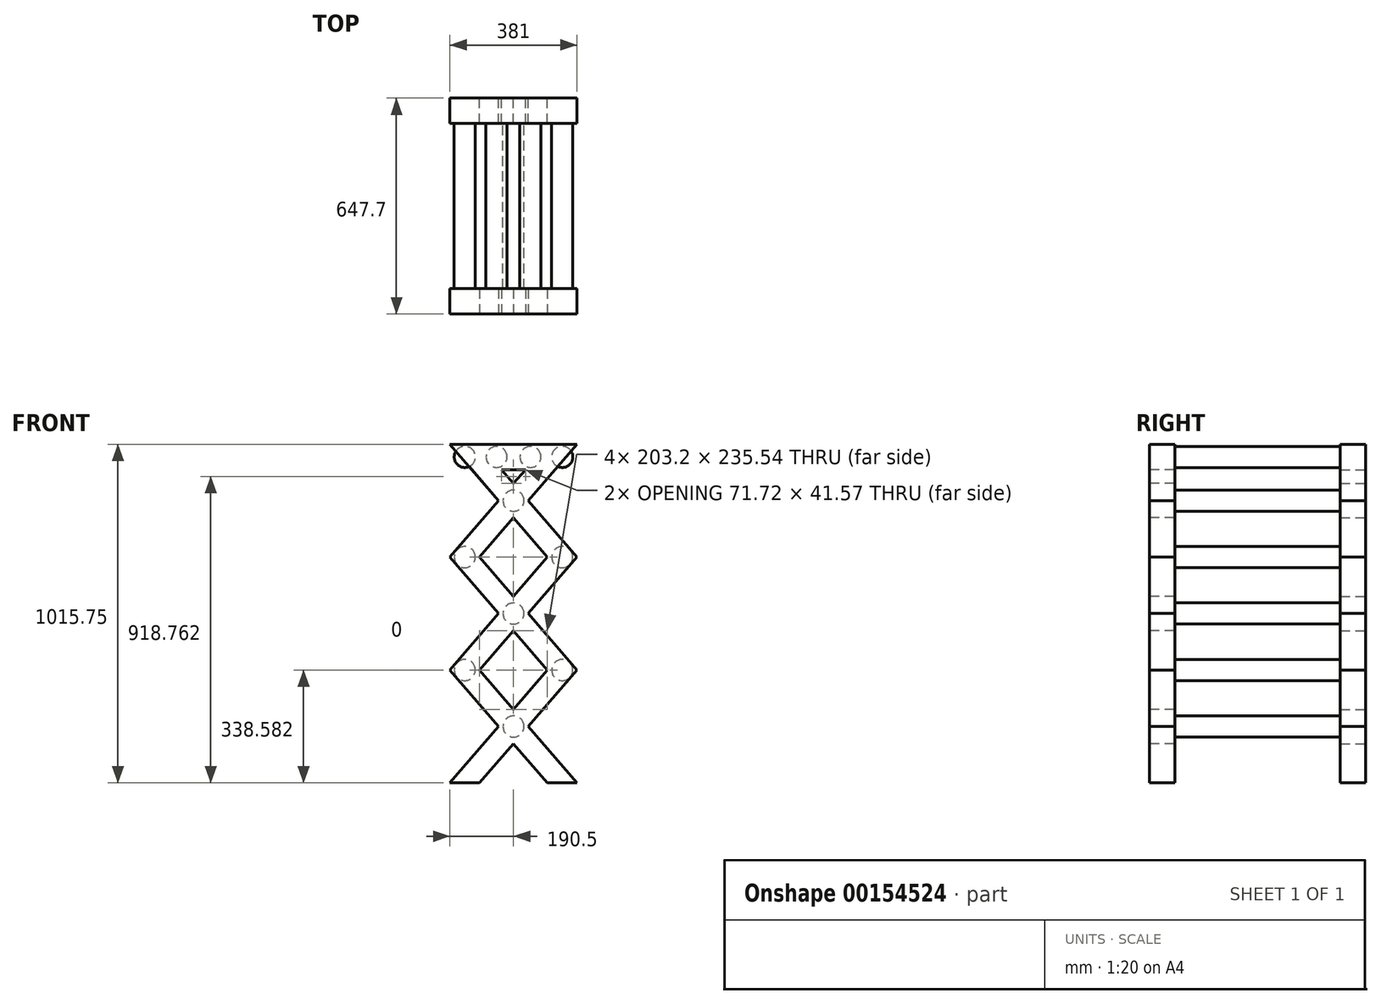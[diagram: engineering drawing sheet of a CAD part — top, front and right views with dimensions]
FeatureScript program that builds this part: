
annotation { "Feature Type Name" : "Feature", "Feature Type Description" : "" }
export const myFeature = defineFeature(function(context is Context, id is Id, definition is map)
    precondition{}
    {
        {
            var Q0;
            Q0=qCreatedBy(makeId("Front.planeOp"),FACE);
            var sketch = newSketch(context, id + "F0", { "sketchPlane" : qUnion([Q0])});
            skLineSegment(sketch, "E0", {"start": v(0, 0) * mm, "end": v(-292.1, 338.58) * mm});
            skLineSegment(sketch, "E1", {"start": v(-292.1, 338.58) * mm, "end": v(-381, 338.58) * mm});
            skLineSegment(sketch, "E2", {"start": v(-381, 338.58) * mm, "end": v(-88.9, 0) * mm});
            skLineSegment(sketch, "E3", {"start": v(-88.9, 0) * mm, "end": v(0, 0) * mm});
            skLineSegment(sketch, "E4", {"start": v(-292.1, 0) * mm, "end": v(0, 338.58) * mm});
            skLineSegment(sketch, "E5", {"start": v(0, 338.58) * mm, "end": v(-88.9, 338.58) * mm});
            skLineSegment(sketch, "E6", {"start": v(-88.9, 338.58) * mm, "end": v(-381, 0) * mm});
            skLineSegment(sketch, "E7", {"start": v(-381, 0) * mm, "end": v(-292.1, 0) * mm});
            skLineSegment(sketch, "E8.MirrorCS", {"start": v(0, 677.16) * mm, "end": v(-292.1, 338.58) * mm});
            skLineSegment(sketch, "E9.MirrorCS", {"start": v(-381, 338.58) * mm, "end": v(-88.9, 677.16) * mm});
            skLineSegment(sketch, "E10.MirrorCS", {"start": v(-88.9, 338.58) * mm, "end": v(-381, 677.16) * mm});
            skLineSegment(sketch, "E11.MirrorCS", {"start": v(-292.1, 677.16) * mm, "end": v(0, 338.58) * mm});
            skLineSegment(sketch, "E12.MirrorCS", {"start": v(-381, 677.16) * mm, "end": v(-292.1, 677.16) * mm});
            skLineSegment(sketch, "E13.MirrorCS", {"start": v(-88.9, 677.16) * mm, "end": v(0, 677.16) * mm});
            skLineSegment(sketch, "E14.MirrorCS", {"start": v(-292.1, 677.16) * mm, "end": v(0, 1015.75) * mm});
            skLineSegment(sketch, "E15.MirrorCS", {"start": v(-88.9, 1015.75) * mm, "end": v(-381, 677.16) * mm});
            skLineSegment(sketch, "E16.MirrorCS", {"start": v(-381, 1015.75) * mm, "end": v(-88.9, 677.16) * mm});
            skLineSegment(sketch, "E17.MirrorCS", {"start": v(0, 677.16) * mm, "end": v(-292.1, 1015.75) * mm});
            skLineSegment(sketch, "E18.MirrorCS", {"start": v(0, 1015.75) * mm, "end": v(-88.9, 1015.75) * mm});
            skLineSegment(sketch, "E19.MirrorCS", {"start": v(-292.1, 1015.75) * mm, "end": v(-381, 1015.75) * mm});
            skLineSegment(sketch, "E20", {"start": v(-292.1, 1015.75) * mm, "end": v(-88.9, 1015.75) * mm});
            skLineSegment(sketch, "E21", {"start": v(-226.36, 939.55) * mm, "end": v(-154.64, 939.55) * mm});
            skSolve(sketch);
        }
        {
            var Q0;
            {var subQ5=sQuery(id+"F0.wireOp",EDGE,"E12.MirrorCS");Q0=makeQuery(id+"F0.imprint","IMPRINT",FACE,{"disambiguationData":[TD([[makeQuery(id+"F0.imprint","IMPRINT",EDGE,{"derivedFrom":subQ5}),-1.0]])]});}
            var Q1;
            {var subQ0=sQuery(id+"F0.wireOp",EDGE,"E11.MirrorCS");var subQ1=sQuery(id+"F0.wireOp",EDGE,"E8.MirrorCS");var subQ2=makeQuery(id+"F0.imprint","INTERSECT",VERTEX,{"derivedFrom":[subQ1,subQ0]});Q1=makeQuery(id+"F0.imprint","IMPRINT",FACE,{"disambiguationData":[TD([[makeQuery(id+"F0.imprint","IMPRINT",EDGE,{"disambiguationData":[TD([[subQ2,-1.0]])],"derivedFrom":subQ1}),-1.0]])]});}
            var Q2;
            {var subQ0=sQuery(id+"F0.wireOp",EDGE,"E13.MirrorCS");Q2=makeQuery(id+"F0.imprint","IMPRINT",FACE,{"disambiguationData":[TD([[makeQuery(id+"F0.imprint","IMPRINT",EDGE,{"derivedFrom":subQ0}),-1.0]])]});}
            var Q3;
            {var subQ0=sQuery(id+"F0.wireOp",EDGE,"E5");Q3=makeQuery(id+"F0.imprint","IMPRINT",FACE,{"disambiguationData":[TD([[makeQuery(id+"F0.imprint","IMPRINT",EDGE,{"derivedFrom":subQ0}),-1.0]])]});}
            var Q4;
            {var subQ0=sQuery(id+"F0.wireOp",EDGE,"E1");Q4=makeQuery(id+"F0.imprint","IMPRINT",FACE,{"disambiguationData":[TD([[makeQuery(id+"F0.imprint","IMPRINT",EDGE,{"derivedFrom":subQ0}),-1.0]])]});}
            var Q5;
            {var subQ0=sQuery(id+"F0.wireOp",EDGE,"E1");Q5=makeQuery(id+"F0.imprint","IMPRINT",FACE,{"disambiguationData":[TD([[makeQuery(id+"F0.imprint","IMPRINT",EDGE,{"derivedFrom":subQ0}),1.0]])]});}
            var Q6;
            {var subQ5=sQuery(id+"F0.wireOp",EDGE,"E5");Q6=makeQuery(id+"F0.imprint","IMPRINT",FACE,{"disambiguationData":[TD([[makeQuery(id+"F0.imprint","IMPRINT",EDGE,{"derivedFrom":subQ5}),1.0]])]});}
            var Q7;
            {var subQ0=sQuery(id+"F0.wireOp",EDGE,"E4");var subQ1=sQuery(id+"F0.wireOp",EDGE,"E0");var subQ2=makeQuery(id+"F0.imprint","INTERSECT",VERTEX,{"derivedFrom":[subQ1,subQ0]});Q7=makeQuery(id+"F0.imprint","IMPRINT",FACE,{"disambiguationData":[TD([[makeQuery(id+"F0.imprint","IMPRINT",EDGE,{"disambiguationData":[TD([[subQ2,-1.0]])],"derivedFrom":subQ1}),1.0]])]});}
            var Q8;
            {var subQ0=sQuery(id+"F0.wireOp",EDGE,"E3");Q8=makeQuery(id+"F0.imprint","IMPRINT",FACE,{"disambiguationData":[TD([[makeQuery(id+"F0.imprint","IMPRINT",EDGE,{"derivedFrom":subQ0}),1.0]])]});}
            var Q9;
            {var subQ5=sQuery(id+"F0.wireOp",EDGE,"E7");Q9=makeQuery(id+"F0.imprint","IMPRINT",FACE,{"disambiguationData":[TD([[makeQuery(id+"F0.imprint","IMPRINT",EDGE,{"derivedFrom":subQ5}),1.0]])]});}
            var Q10;
            {var subQ0=sQuery(id+"F0.wireOp",EDGE,"UBlNaQ5L-5llw-cMuU-o5Na-Ca1wuriGQUsm");Q10=makeQuery(id+"F0.imprint","IMPRINT",FACE,{"disambiguationData":[TD([[makeQuery(id+"F0.imprint","IMPRINT",EDGE,{"derivedFrom":subQ0}),1.0]])]});}
            var Q11;
            {var subQ0=sQuery(id+"F0.wireOp",EDGE,"E12.MirrorCS");Q11=makeQuery(id+"F0.imprint","IMPRINT",FACE,{"disambiguationData":[TD([[makeQuery(id+"F0.imprint","IMPRINT",EDGE,{"derivedFrom":subQ0}),1.0]])]});}
            var Q12;
            {var subQ0=sQuery(id+"F0.wireOp",EDGE,"E17.MirrorCS");var subQ1=sQuery(id+"F0.wireOp",EDGE,"E14.MirrorCS");var subQ2=makeQuery(id+"F0.imprint","INTERSECT",VERTEX,{"derivedFrom":[subQ1,subQ0]});Q12=makeQuery(id+"F0.imprint","IMPRINT",FACE,{"disambiguationData":[TD([[makeQuery(id+"F0.imprint","IMPRINT",EDGE,{"disambiguationData":[TD([[subQ2,1.0]])],"derivedFrom":subQ1}),1.0]])]});}
            var Q13;
            {var subQ0=sQuery(id+"F0.wireOp",EDGE,"E13.MirrorCS");Q13=makeQuery(id+"F0.imprint","IMPRINT",FACE,{"disambiguationData":[TD([[makeQuery(id+"F0.imprint","IMPRINT",EDGE,{"derivedFrom":subQ0}),1.0]])]});}
            var Q14;
            {var subQ6=sQuery(id+"F0.wireOp",EDGE,"E18.MirrorCS");Q14=makeQuery(id+"F0.imprint","IMPRINT",FACE,{"disambiguationData":[TD([[makeQuery(id+"F0.imprint","IMPRINT",EDGE,{"derivedFrom":subQ6}),1.0]])]});}
            var Q15;
            {var subQ0=sQuery(id+"F0.wireOp",EDGE,"E20");Q15=makeQuery(id+"F0.imprint","IMPRINT",FACE,{"disambiguationData":[TD([[makeQuery(id+"F0.imprint","IMPRINT",EDGE,{"derivedFrom":subQ0}),-1.0]])]});}
            var Q16;
            {var subQ0=sQuery(id+"F0.wireOp",EDGE,"E19.MirrorCS");Q16=makeQuery(id+"F0.imprint","IMPRINT",FACE,{"disambiguationData":[TD([[makeQuery(id+"F0.imprint","IMPRINT",EDGE,{"derivedFrom":subQ0}),1.0]])]});}
            extrude(context, id + "F1", {"entities" : qUnion([Q0, Q1, Q2, Q3, Q4, Q5, Q6, Q7, Q8, Q9, Q10, Q11, Q12, Q13, Q14, Q15, Q16]), "depth" : 76.2 * mm});
        }
        {
            var Q0;
            Q0=makeQuery(id+"F1.opExtrude","CAP_FACE",FACE,{"disambiguationData":[OSD([sQuery(id+"F0.wireOp",EDGE,"E0"),sQuery(id+"F0.wireOp",EDGE,"E2"),sQuery(id+"F0.wireOp",EDGE,"E3"),sQuery(id+"F0.wireOp",EDGE,"E4"),sQuery(id+"F0.wireOp",EDGE,"E6"),sQuery(id+"F0.wireOp",EDGE,"E7"),sQuery(id+"F0.wireOp",EDGE,"E8.MirrorCS"),sQuery(id+"F0.wireOp",EDGE,"E9.MirrorCS"),sQuery(id+"F0.wireOp",EDGE,"E10.MirrorCS"),sQuery(id+"F0.wireOp",EDGE,"E11.MirrorCS"),sQuery(id+"F0.wireOp",EDGE,"E12.MirrorCS"),sQuery(id+"F0.wireOp",EDGE,"E13.MirrorCS"),sQuery(id+"F0.wireOp",EDGE,"UBlNaQ5L-5llw-cMuU-o5Na-Ca1wuriGQUsm"),sQuery(id+"F0.wireOp",EDGE,"YSf9pvNf-J0qR-IQ9T-Leeb-qLKvmh4iDBAS")])],"isStart":false});
            var sketch = newSketch(context, id + "F2", { "sketchPlane" : qUnion([Q0])});
            skCircle(sketch, "E22", {"center": v(-336.55, 677.16) * mm, "radius": 31.75 * mm});
            skCircle(sketch, "E23", {"center": v(-44.45, 677.16) * mm, "radius": 31.75 * mm});
            skCircle(sketch, "E24", {"center": v(-190.5, 507.87) * mm, "radius": 31.75 * mm});
            skCircle(sketch, "E25", {"center": v(-190.5, 169.3) * mm, "radius": 31.75 * mm});
            skCircle(sketch, "E26", {"center": v(-44.45, 338.58) * mm, "radius": 31.75 * mm});
            skCircle(sketch, "E27", {"center": v(-336.55, 338.58) * mm, "radius": 31.75 * mm});
            skCircle(sketch, "E28", {"center": v(-190.5, 846.45) * mm, "radius": 31.75 * mm});
            skCircle(sketch, "E29", {"center": v(-44.45, 977.65) * mm, "radius": 31.75 * mm});
            skCircle(sketch, "E30", {"center": v(-139.7, 977.65) * mm, "radius": 31.75 * mm});
            skCircle(sketch, "E31", {"center": v(-336.55, 977.65) * mm, "radius": 31.75 * mm});
            skCircle(sketch, "E32", {"center": v(-241.3, 977.65) * mm, "radius": 31.75 * mm});
            skLineSegment(sketch, "E33", {"start": v(-190.5, 897.98) * mm, "end": v(-190.5, 794.93) * mm, "construction": true});
            skLineSegment(sketch, "E34", {"start": v(-190.5, 794.93) * mm, "end": v(-190.5, 559.4) * mm, "construction": true});
            skLineSegment(sketch, "E35", {"start": v(-190.5, 559.4) * mm, "end": v(-190.5, 456.35) * mm, "construction": true});
            skLineSegment(sketch, "E36", {"start": v(-190.5, 456.35) * mm, "end": v(-190.5, 220.81) * mm, "construction": true});
            skLineSegment(sketch, "E37", {"start": v(-190.5, 220.81) * mm, "end": v(-190.5, 117.77) * mm, "construction": true});
            skLineSegment(sketch, "E38", {"start": v(0, 338.58) * mm, "end": v(-88.9, 338.58) * mm, "construction": true});
            skLineSegment(sketch, "E39", {"start": v(-292.1, 338.58) * mm, "end": v(-381, 338.58) * mm, "construction": true});
            skLineSegment(sketch, "E40", {"start": v(0, 677.16) * mm, "end": v(-88.9, 677.16) * mm, "construction": true});
            skLineSegment(sketch, "E41", {"start": v(-88.9, 677.16) * mm, "end": v(-292.1, 677.16) * mm, "construction": true});
            skLineSegment(sketch, "E42", {"start": v(-292.1, 677.16) * mm, "end": v(-381, 677.16) * mm, "construction": true});
            skLineSegment(sketch, "E43", {"start": v(-190.5, 939.55) * mm, "end": v(-190.5, 1015.75) * mm, "construction": true});
            skLineSegment(sketch, "E44", {"start": v(-190.5, 977.65) * mm, "end": v(-348.13, 977.65) * mm, "construction": true});
            skLineSegment(sketch, "E45", {"start": v(-190.5, 977.65) * mm, "end": v(-32.87, 977.65) * mm, "construction": true});
            skSolve(sketch);
        }
        {
            var Q0;
            Q0 = qSketchRegion(id + "F2", true);
            extrude(context, id + "F3", {"entities" : qUnion([Q0]), "operationType" : NewBodyOperationType.ADD, "depth" : 247.65 * mm});
        }
        {
            var Q0;
            Q0=makeQuery(id+"F1.opExtrude","SWEPT_BODY",BODY,{"disambiguationData":[OSD([sQuery(id+"F0.wireOp",EDGE,"E0"),sQuery(id+"F0.wireOp",EDGE,"E2"),sQuery(id+"F0.wireOp",EDGE,"E3"),sQuery(id+"F0.wireOp",EDGE,"E4"),sQuery(id+"F0.wireOp",EDGE,"E6"),sQuery(id+"F0.wireOp",EDGE,"E7"),sQuery(id+"F0.wireOp",EDGE,"E8.MirrorCS"),sQuery(id+"F0.wireOp",EDGE,"E9.MirrorCS"),sQuery(id+"F0.wireOp",EDGE,"E10.MirrorCS"),sQuery(id+"F0.wireOp",EDGE,"E11.MirrorCS"),sQuery(id+"F0.wireOp",EDGE,"E14.MirrorCS"),sQuery(id+"F0.wireOp",EDGE,"E15.MirrorCS"),sQuery(id+"F0.wireOp",EDGE,"E16.MirrorCS"),sQuery(id+"F0.wireOp",EDGE,"E17.MirrorCS"),sQuery(id+"F0.wireOp",EDGE,"E18.MirrorCS"),sQuery(id+"F0.wireOp",EDGE,"E19.MirrorCS"),sQuery(id+"F0.wireOp",EDGE,"E20"),sQuery(id+"F0.wireOp",EDGE,"E21")])]});
            var Q1;
            Q1=makeQuery(id+"F3.opExtrude","CAP_FACE",FACE,{"disambiguationData":[OSD([sQuery(id+"F2.wireOp",EDGE,"E31")])],"isStart":false});
            mirror(context, id + "F4", {"operationType" : NewBodyOperationType.ADD, "entities" : qUnion([Q0]), "mirrorPlane" : qUnion([Q1])});
        }
    });
